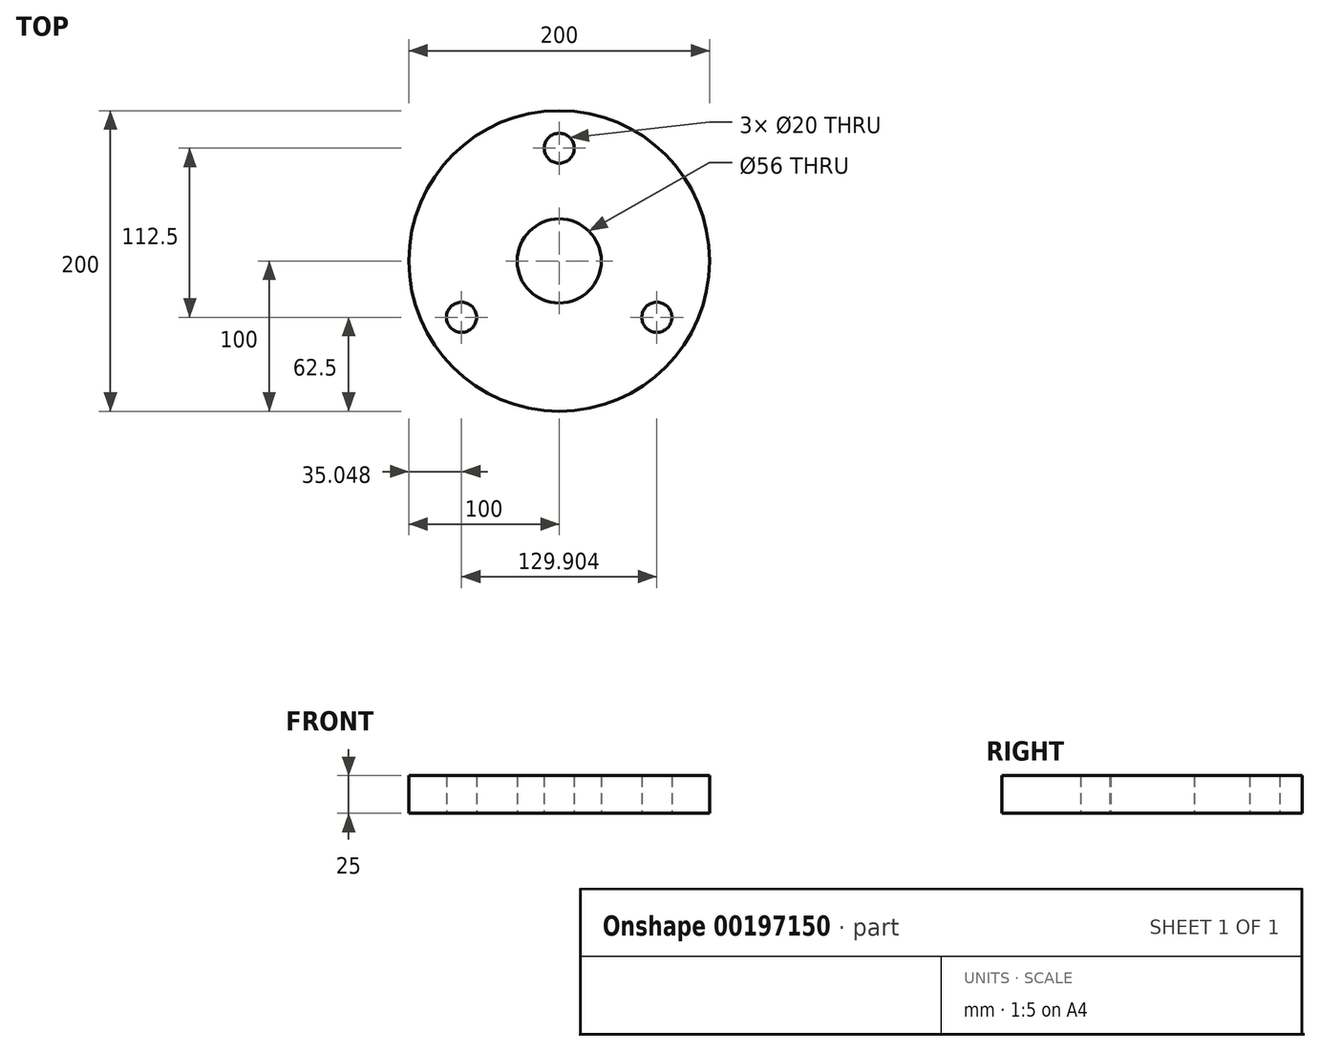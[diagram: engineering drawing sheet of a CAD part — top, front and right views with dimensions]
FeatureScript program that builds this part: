
annotation { "Feature Type Name" : "Feature", "Feature Type Description" : "" }
export const myFeature = defineFeature(function(context is Context, id is Id, definition is map)
    precondition{}
    {
        {
            var Q0;
            Q0=qCreatedBy(makeId("Top.planeOp"),FACE);
            var sketch = newSketch(context, id + "F0", { "sketchPlane" : qUnion([Q0])});
            skCircle(sketch, "E0", {"center": v(0, 0) * mm, "radius": 28 * mm});
            skCircle(sketch, "E1", {"center": v(0, 0) * mm, "radius": 100 * mm});
            skLineSegment(sketch, "E2", {"start": v(0, 0) * mm, "end": v(0, 75) * mm, "construction": true});
            skCircle(sketch, "E3", {"center": v(0, 75) * mm, "radius": 10 * mm});
            skCircle(sketch, "E4.1.0", {"center": v(-64.95, -37.5) * mm, "radius": 10 * mm});
            skCircle(sketch, "E4.2.0", {"center": v(64.95, -37.5) * mm, "radius": 10 * mm});
            skSolve(sketch);
        }
        {
            var Q0;
            Q0 = qSketchRegion(id + "F0", true);
            extrude(context, id + "F1", {"entities" : qUnion([Q0]), "depth" : 25 * mm});
        }
    });
